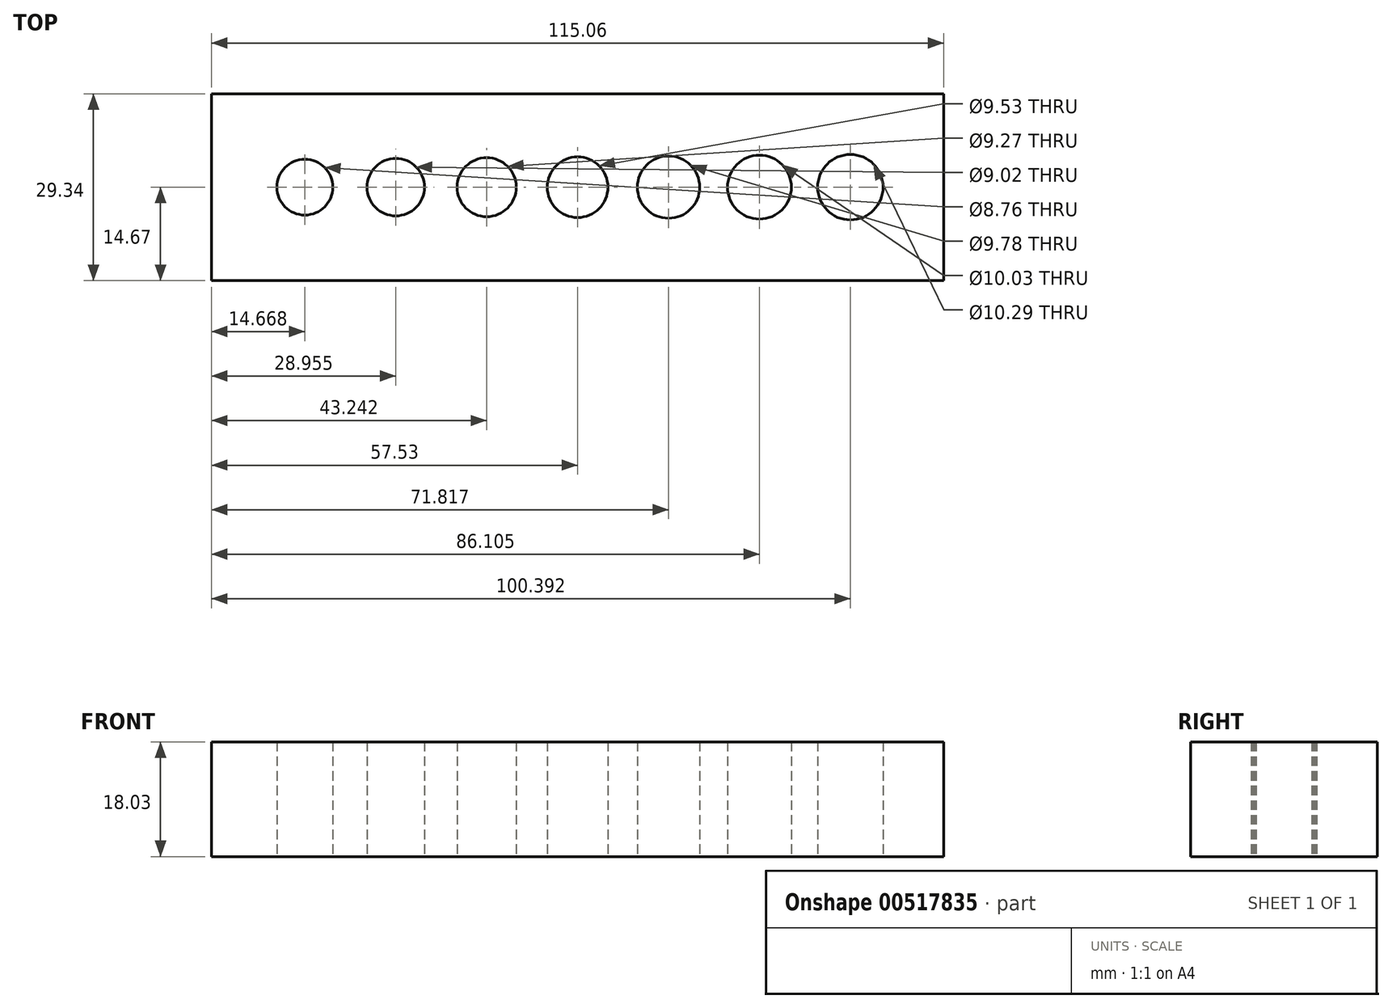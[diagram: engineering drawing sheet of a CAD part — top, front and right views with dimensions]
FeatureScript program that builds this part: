
annotation { "Feature Type Name" : "Feature", "Feature Type Description" : "" }
export const myFeature = defineFeature(function(context is Context, id is Id, definition is map)
    precondition{}
    {
        {
            var Q0;
            Q0=qCreatedBy(makeId("Top.planeOp"),FACE);
            var sketch = newSketch(context, id + "F0", { "sketchPlane" : qUnion([Q0])});
            skCircle(sketch, "E0", {"center": v(0, 0) * mm, "radius": 4.76 * mm});
            skCircle(sketch, "E1", {"center": v(-14.29, 0) * mm, "radius": 4.64 * mm});
            skCircle(sketch, "E2", {"center": v(-28.58, 0) * mm, "radius": 4.5 * mm});
            skCircle(sketch, "E3", {"center": v(-42.86, 0) * mm, "radius": 4.38 * mm});
            skCircle(sketch, "E4", {"center": v(14.29, 0) * mm, "radius": 4.89 * mm});
            skCircle(sketch, "E5", {"center": v(28.58, 0) * mm, "radius": 5.02 * mm});
            skCircle(sketch, "E6", {"center": v(42.86, 0) * mm, "radius": 5.14 * mm});
            skLineSegment(sketch, "E7", {"start": v(-42.86, 0) * mm, "end": v(-28.58, 0) * mm, "construction": true});
            skLineSegment(sketch, "E8", {"start": v(-28.58, 0) * mm, "end": v(-14.29, 0) * mm, "construction": true});
            skLineSegment(sketch, "E9", {"start": v(0, 0) * mm, "end": v(14.29, 0) * mm, "construction": true});
            skLineSegment(sketch, "E10", {"start": v(28.58, 0) * mm, "end": v(42.86, 0) * mm, "construction": true});
            skLineSegment(sketch, "E11", {"start": v(28.58, 0) * mm, "end": v(14.29, 0) * mm, "construction": true});
            skLineSegment(sketch, "E12", {"start": v(0, 0) * mm, "end": v(-14.29, 0) * mm, "construction": true});
            skLineSegment(sketch, "E13.bottom", {"start": v(57.53, -14.67) * mm, "end": v(-57.53, -14.67) * mm});
            skLineSegment(sketch, "E13.top", {"start": v(57.53, 14.67) * mm, "end": v(-57.53, 14.67) * mm});
            skLineSegment(sketch, "E13.left", {"start": v(57.53, -14.67) * mm, "end": v(57.53, 14.67) * mm});
            skLineSegment(sketch, "E13.right", {"start": v(-57.53, -14.67) * mm, "end": v(-57.53, 14.67) * mm});
            skCircle(sketch, "E14", {"center": v(-13.8, 29.2) * mm, "radius": 5.75 * mm});
            skCircle(sketch, "E15", {"center": v(-13.8, 29.2) * mm, "radius": 4.76 * mm});
            skSolve(sketch);
        }
        {
            var Q0;
            Q0=makeQuery(id+"F0.imprint","IMPRINT",FACE,{"disambiguationData":[TD([[makeQuery(id+"F0.imprint","IMPRINT",EDGE,{"derivedFrom":sQuery(id+"F0.wireOp",EDGE,"E0")}),-1.0]])]});
            extrude(context, id + "F1", {"entities" : qUnion([Q0]), "depth" : 18.03 * mm, "offsetDistance" : 25 * mm});
        }
    });
